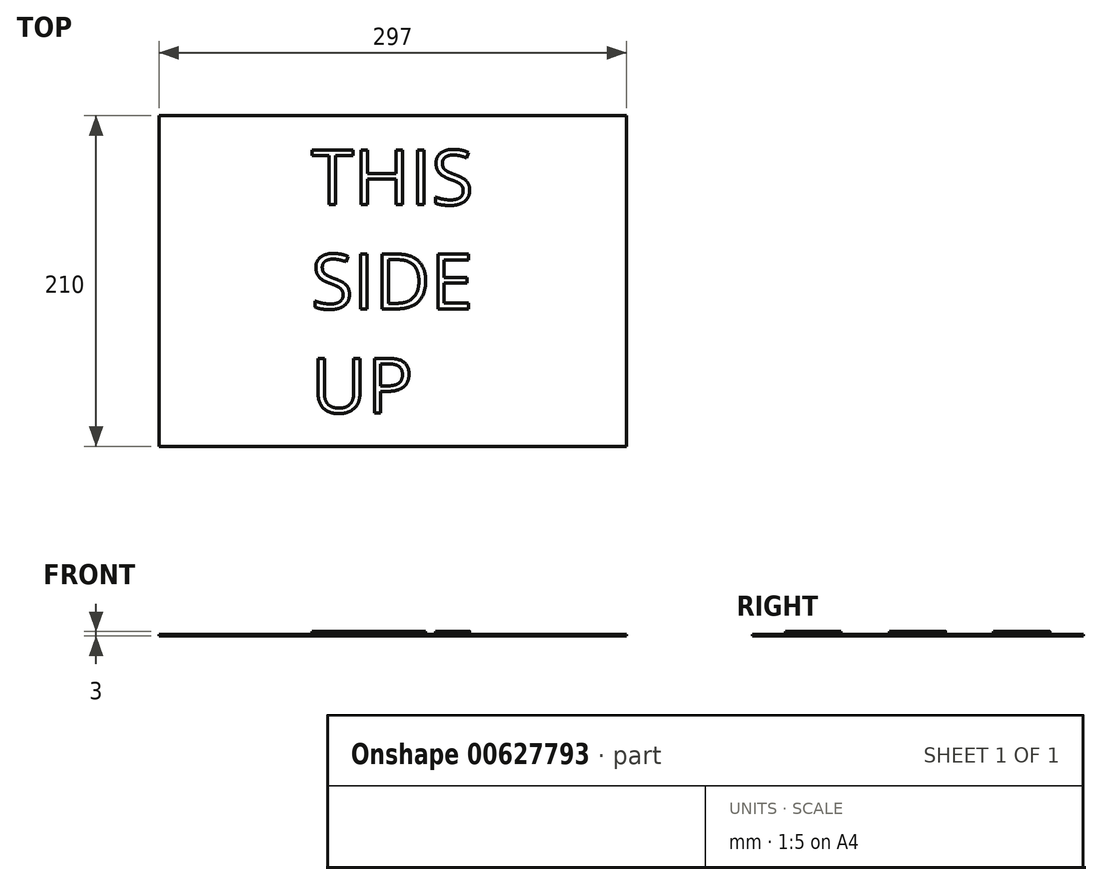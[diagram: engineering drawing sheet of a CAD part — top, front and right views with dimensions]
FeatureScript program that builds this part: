
annotation { "Feature Type Name" : "Feature", "Feature Type Description" : "" }
export const myFeature = defineFeature(function(context is Context, id is Id, definition is map)
    precondition{}
    {
        {
            var Q0;
            Q0=qCreatedBy(makeId("Top.planeOp"),FACE);
            var sketch = newSketch(context, id + "F0", { "sketchPlane" : qUnion([Q0])});
            skLineSegment(sketch, "E0.bottom", {"start": v(-251.93, 163.61) * mm, "end": v(45.07, 163.61) * mm});
            skLineSegment(sketch, "E0.top", {"start": v(-251.93, -46.39) * mm, "end": v(45.07, -46.39) * mm});
            skLineSegment(sketch, "E0.left", {"start": v(-251.93, 163.61) * mm, "end": v(-251.93, -46.39) * mm});
            skLineSegment(sketch, "E0.right", {"start": v(45.07, 163.61) * mm, "end": v(45.07, -46.39) * mm});
            skSolve(sketch);
        }
        {
            var Q0;
            Q0=makeQuery(id+"F0.imprint","IMPRINT",FACE,{"disambiguationData":[TD([[makeQuery(id+"F0.imprint","IMPRINT",EDGE,{"derivedFrom":sQuery(id+"F0.wireOp",EDGE,"E0.bottom")}),-1.0]])]});
            extrude(context, id + "F1", {"entities" : qUnion([Q0]), "depth" : 1 * mm, "offsetDistance" : 25 * mm});
        }
        {
            var Q0;
            Q0=makeQuery(id+"F1.opExtrude","CAP_FACE",FACE,{"disambiguationData":[OSD([sQuery(id+"F0.wireOp",EDGE,"E0.bottom"),sQuery(id+"F0.wireOp",EDGE,"E0.top"),sQuery(id+"F0.wireOp",EDGE,"E0.left"),sQuery(id+"F0.wireOp",EDGE,"E0.right")])],"isStart":false});
            var sketch = newSketch(context, id + "F2", { "sketchPlane" : qUnion([Q0])});
            skText(sketch, "E1", { "text": "THIS\nSIDE\nUP", "fontName": "OpenSans-Regular.ttf"});
            const initialGuessF2  = {"E1": [-0.15533, 0.1071, 1, 0, 0.035]};
            skSetInitialGuess(sketch, initialGuessF2);
            skSolve(sketch);
        }
        {
            var Q0;
            Q0 = qSketchRegion(id + "F2", true);
            extrude(context, id + "F3", {"entities" : qUnion([Q0]), "operationType" : NewBodyOperationType.ADD, "depth" : 2 * mm, "offsetDistance" : 25 * mm});
        }
    });
